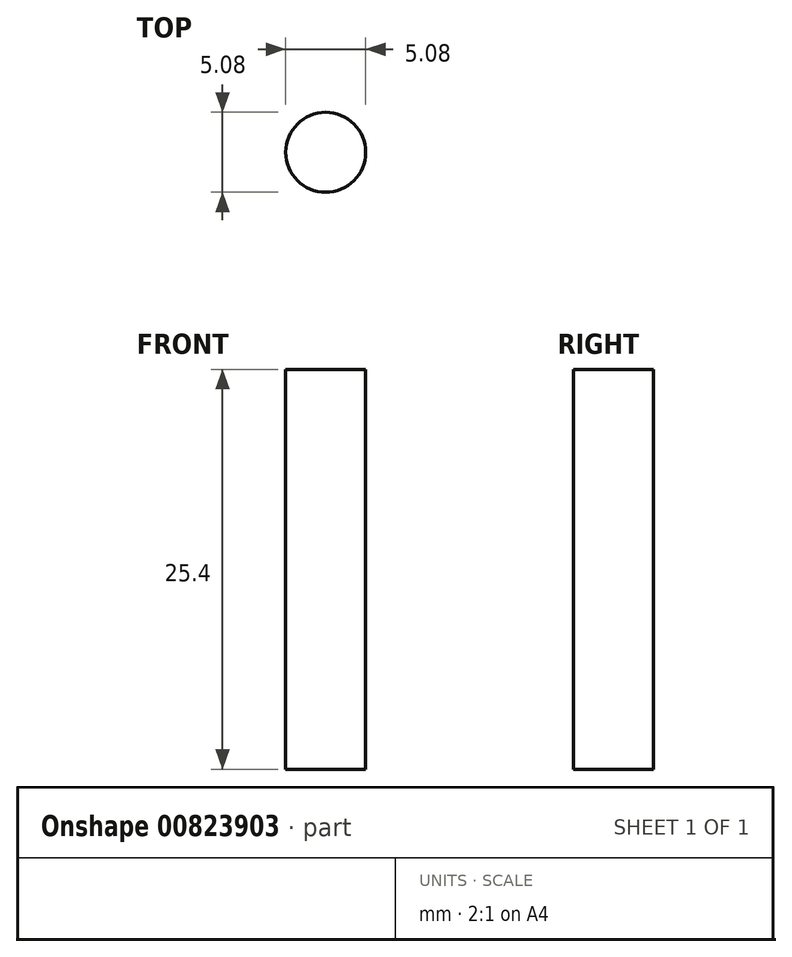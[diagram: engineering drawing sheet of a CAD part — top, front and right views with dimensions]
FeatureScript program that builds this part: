
annotation { "Feature Type Name" : "Feature", "Feature Type Description" : "" }
export const myFeature = defineFeature(function(context is Context, id is Id, definition is map)
    precondition{}
    {
        {
            var Q0;
            Q0=qCreatedBy(makeId("Top.planeOp"),FACE);
            var sketch = newSketch(context, id + "F0", { "sketchPlane" : qUnion([Q0])});
            skCircle(sketch, "E0", {"center": v(0, 0) * mm, "radius": 2.54 * mm});
            skSolve(sketch);
        }
        {
            var Q0;
            Q0 = qSketchRegion(id + "F0", true);
            extrude(context, id + "F1", {"entities" : qUnion([Q0]), "depth" : 25.4 * mm, "offsetDistance" : 25.4 * mm});
        }
    });
